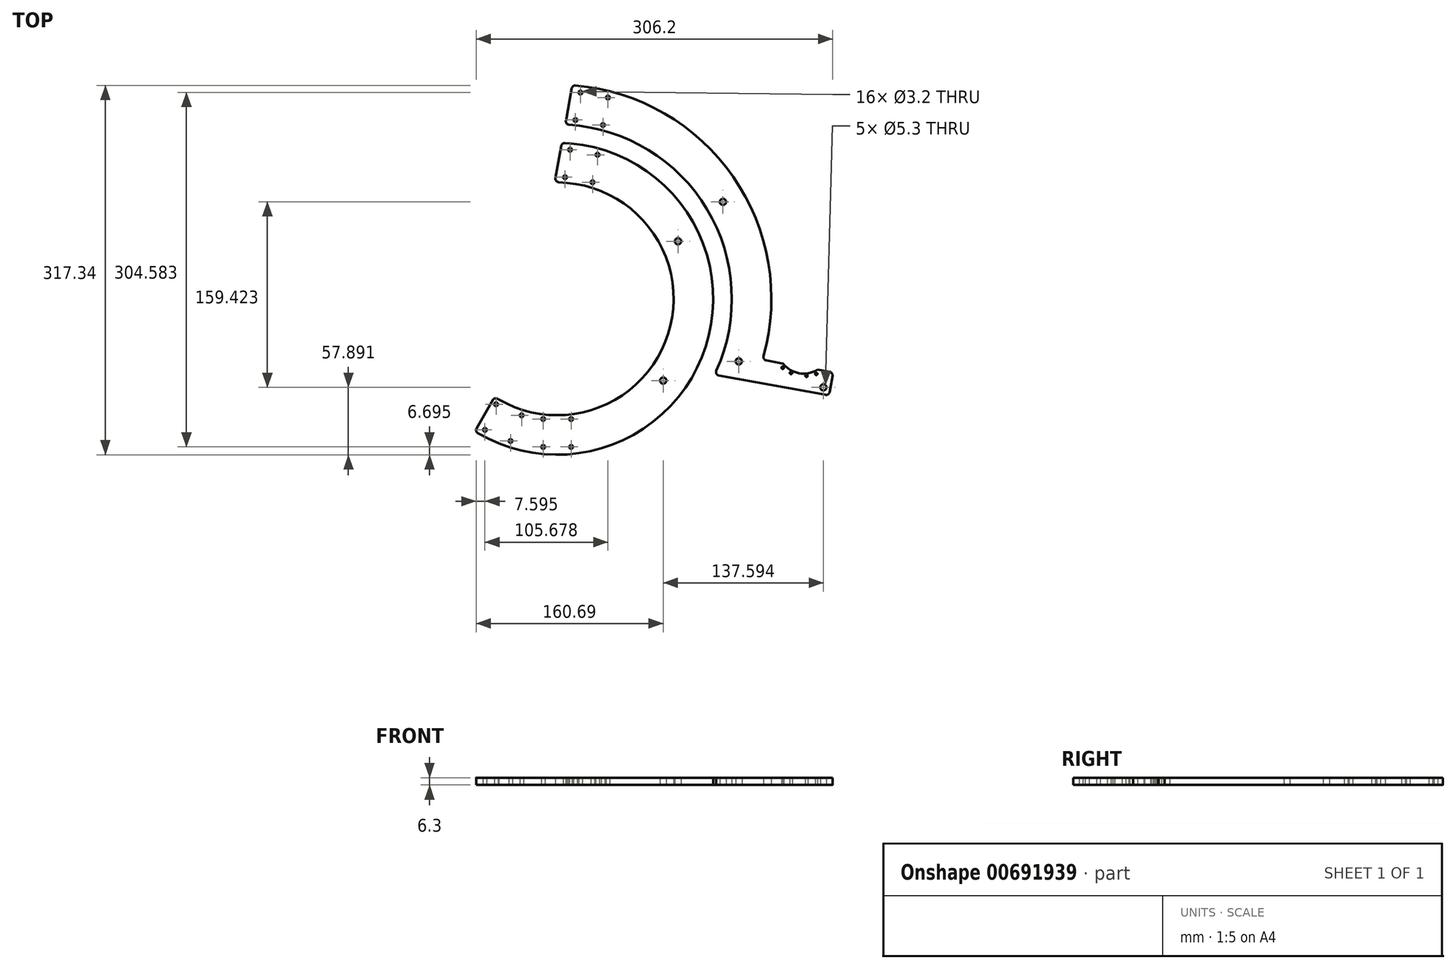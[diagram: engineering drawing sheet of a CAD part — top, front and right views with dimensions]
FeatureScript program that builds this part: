
annotation { "Feature Type Name" : "Feature", "Feature Type Description" : "" }
export const myFeature = defineFeature(function(context is Context, id is Id, definition is map)
    precondition{}
    {
        {
            var Q0;
            Q0=qCreatedBy(makeId("Top.planeOp"),FACE);
            var sketch = newSketch(context, id + "F0", { "sketchPlane" : qUnion([Q0])});
            skArc(sketch, "E0", {"start": v(-50, -86.6) * mm, "mid": v(95.37, -30.07) * mm, "end": v(8.72, 99.62) * mm});
            skLineSegment(sketch, "E1", {"start": v(11.68, 133.5) * mm, "end": v(0, 0) * mm, "construction": true});
            skLineSegment(sketch, "E2", {"start": v(-67, -116.05) * mm, "end": v(0, 0) * mm, "construction": true});
            skArc(sketch, "E3", {"start": v(11.68, 133.5) * mm, "mid": v(127.6, -40.94) * mm, "end": v(-68.16, -115.37) * mm});
            skLineSegment(sketch, "E4", {"start": v(0, 0) * mm, "end": v(-141.6, -325.67) * mm, "construction": true});
            skLineSegment(sketch, "E5", {"start": v(0, 0) * mm, "end": v(56.94, 313.3) * mm, "construction": true});
            skCircle(sketch, "E6", {"center": v(-52.47, -90.59) * mm, "radius": 1.6 * mm});
            skCircle(sketch, "E7", {"center": v(-62.04, -112.6) * mm, "radius": 1.6 * mm});
            skCircle(sketch, "E8", {"center": v(-30.47, -100.16) * mm, "radius": 1.6 * mm});
            skCircle(sketch, "E9", {"center": v(-40.04, -122.17) * mm, "radius": 1.6 * mm});
            skLineSegment(sketch, "E10", {"start": v(-76.38, -80.2) * mm, "end": v(-0.38, -113.24) * mm, "construction": true});
            skLineSegment(sketch, "E11", {"start": v(-90.91, -100.05) * mm, "end": v(-6.32, -136.83) * mm, "construction": true});
            skLineSegment(sketch, "E12", {"start": v(-105.1, -211.63) * mm, "end": v(-88.22, -172.8) * mm, "construction": true});
            skLineSegment(sketch, "E13", {"start": v(-83.02, -221.03) * mm, "end": v(-61.96, -172.6) * mm, "construction": true});
            skLineSegment(sketch, "E14", {"start": v(6.07, 129) * mm, "end": v(53.18, 120.43) * mm, "construction": true});
            skLineSegment(sketch, "E15", {"start": v(3.55, 105.06) * mm, "end": v(50.74, 96.48) * mm, "construction": true});
            skLineSegment(sketch, "E16", {"start": v(54.37, 232.05) * mm, "end": v(48.26, 198.43) * mm, "construction": true});
            skLineSegment(sketch, "E17", {"start": v(30.52, 235.08) * mm, "end": v(24.48, 201.84) * mm, "construction": true});
            skCircle(sketch, "E18", {"center": v(6.79, 104.47) * mm, "radius": 1.6 * mm});
            skCircle(sketch, "E19", {"center": v(30.4, 100.18) * mm, "radius": 1.6 * mm});
            skCircle(sketch, "E20", {"center": v(34.7, 123.8) * mm, "radius": 1.6 * mm});
            skCircle(sketch, "E21", {"center": v(11.08, 128.08) * mm, "radius": 1.6 * mm});
            skLineSegment(sketch, "E22", {"start": v(-50.4, -86.35) * mm, "end": v(-50, -86.6) * mm});
            skPoint(sketch, "E23.visualSharp", {"position": v(-53.75, -84.2) * mm});
            skLineSegment(sketch, "E24", {"start": v(11.68, 133.5) * mm, "end": v(6.78, 133.92) * mm});
            skLineSegment(sketch, "E25", {"start": v(3.56, 131.47) * mm, "end": v(-1.46, 103.8) * mm});
            skLineSegment(sketch, "E26", {"start": v(1.23, 100.27) * mm, "end": v(8.72, 99.62) * mm});
            skPoint(sketch, "E27.visualSharp", {"position": v(-2.05, 100.56) * mm});
            skArc(sketch, "E27.filletArc", {"start": v(-1.46, 103.8) * mm, "mid": v(-0.9, 101.44) * mm, "end": v(1.23, 100.27) * mm});
            skPoint(sketch, "E28.visualSharp", {"position": v(4.05, 134.16) * mm});
            skArc(sketch, "E28.filletArc", {"start": v(6.78, 133.92) * mm, "mid": v(4.7, 133.32) * mm, "end": v(3.56, 131.47) * mm});
            skPoint(sketch, "E29.visualSharp", {"position": v(-67, -116.05) * mm});
            skCircle(sketch, "E30", {"center": v(12, -103.3) * mm, "radius": 1.6 * mm});
            skCircle(sketch, "E31", {"center": v(12, -127.3) * mm, "radius": 1.6 * mm});
            skCircle(sketch, "E32.MirrorC", {"center": v(-12, -103.3) * mm, "radius": 1.6 * mm});
            skCircle(sketch, "E33.MirrorC", {"center": v(-12, -127.3) * mm, "radius": 1.6 * mm});
            skLineSegment(sketch, "E34", {"start": v(-69.24, -111.3) * mm, "end": v(-55.32, -86.94) * mm});
            skLineSegment(sketch, "E35", {"start": v(-50.4, -86.35) * mm, "end": v(-51.09, -85.9) * mm});
            skPoint(sketch, "E36.visualSharp", {"position": v(-70.7, -113.84) * mm});
            skArc(sketch, "E36.filletArc", {"start": v(-69.24, -111.3) * mm, "mid": v(-69.54, -113.55) * mm, "end": v(-68.16, -115.37) * mm});
            skArc(sketch, "E37.filletArc", {"start": v(-51.09, -85.9) * mm, "mid": v(-53.42, -85.51) * mm, "end": v(-55.32, -86.94) * mm});
            skCircle(sketch, "E38", {"center": v(103.82, 49.47) * mm, "radius": 2.65 * mm});
            skCircle(sketch, "E39", {"center": v(91.05, -70.25) * mm, "radius": 2.65 * mm});
            skSolve(sketch);
        }
        {
            var Q0;
            {var subQ0=sQuery(id+"F0.wireOp",EDGE,"E0");Q0=makeQuery(id+"F0.imprint","IMPRINT",FACE,{"disambiguationData":[TD([[makeQuery(id+"F0.imprint","IMPRINT",EDGE,{"derivedFrom":subQ0}),-1.0]])]});}
            var Q1;
            {var subQ1=sQuery(id+"F0.wireOp",EDGE,"5APrBCez-5t1e-EGUt-UYpU-bVJNniEtidSN");Q1=makeQuery(id+"F0.imprint","IMPRINT",FACE,{"disambiguationData":[TD([[makeQuery(id+"F0.imprint","IMPRINT",EDGE,{"derivedFrom":subQ1}),-1.0]])]});}
            var Q2;
            {var subQ7=sQuery(id+"F0.wireOp",EDGE,"E24");Q2=makeQuery(id+"F0.imprint","IMPRINT",FACE,{"disambiguationData":[TD([[makeQuery(id+"F0.imprint","IMPRINT",EDGE,{"derivedFrom":subQ7}),1.0]])]});}
            var Q3;
            {var subQ5=sQuery(id+"F0.wireOp",EDGE,"E22");Q3=makeQuery(id+"F0.imprint","IMPRINT",FACE,{"disambiguationData":[TD([[makeQuery(id+"F0.imprint","IMPRINT",EDGE,{"derivedFrom":subQ5}),-1.0]])]});}
            extrude(context, id + "F1", {"entities" : qUnion([Q0, Q1, Q2, Q3]), "depth" : 6.3 * mm, "offsetDistance" : 25 * mm});
        }
        {
            var Q0;
            Q0=qCreatedBy(makeId("Top.planeOp"),FACE);
            var sketch = newSketch(context, id + "F2", { "sketchPlane" : qUnion([Q0])});
            skArc(sketch, "E40", {"start": v(10.26, 149.65) * mm, "mid": v(128.72, 77.01) * mm, "end": v(136.72, -61.71) * mm});
            skArc(sketch, "E41.0", {"start": v(15.75, 183.32) * mm, "mid": v(151.12, 104.98) * mm, "end": v(177.3, -49.22) * mm});
            skLineSegment(sketch, "E42", {"start": v(12.54, 180.87) * mm, "end": v(7.5, 153.18) * mm});
            skLineSegment(sketch, "E43", {"start": v(138.91, -65.9) * mm, "end": v(230.52, -82.55) * mm});
            skLineSegment(sketch, "E44", {"start": v(234.01, -80.13) * mm, "end": v(236.51, -66.36) * mm});
            skLineSegment(sketch, "E45", {"start": v(234.1, -62.87) * mm, "end": v(223.5, -60.94) * mm});
            skArc(sketch, "E46", {"start": v(193.98, -55.58) * mm, "mid": v(207.71, -63.9) * mm, "end": v(223.5, -60.94) * mm});
            skPoint(sketch, "E47.visualSharp", {"position": v(233.48, -83.08) * mm});
            skArc(sketch, "E47.filletArc", {"start": v(230.52, -82.55) * mm, "mid": v(232.77, -82.06) * mm, "end": v(234.01, -80.13) * mm});
            skPoint(sketch, "E48.visualSharp", {"position": v(237.05, -63.4) * mm});
            skArc(sketch, "E48.filletArc", {"start": v(236.51, -66.36) * mm, "mid": v(236.03, -64.11) * mm, "end": v(234.1, -62.87) * mm});
            skPoint(sketch, "E49.visualSharp", {"position": v(135.09, -65.2) * mm});
            skArc(sketch, "E49.filletArc", {"start": v(136.72, -61.71) * mm, "mid": v(136.8, -64.34) * mm, "end": v(138.91, -65.9) * mm});
            skArc(sketch, "E50.filletArc", {"start": v(177.3, -49.22) * mm, "mid": v(177.64, -51.62) * mm, "end": v(179.65, -52.98) * mm});
            skPoint(sketch, "E51.visualSharp", {"position": v(6.9, 149.84) * mm});
            skArc(sketch, "E51.filletArc", {"start": v(7.5, 153.18) * mm, "mid": v(8.1, 150.8) * mm, "end": v(10.26, 149.65) * mm});
            skPoint(sketch, "E52.visualSharp", {"position": v(13.03, 183.54) * mm});
            skArc(sketch, "E52.filletArc", {"start": v(15.75, 183.32) * mm, "mid": v(13.67, 182.72) * mm, "end": v(12.54, 180.87) * mm});
            skLineSegment(sketch, "E53", {"start": v(0, 0) * mm, "end": v(288.03, -52.34) * mm, "construction": true});
            skLineSegment(sketch, "E54", {"start": v(172.85, -31.41) * mm, "end": v(241, -43.8) * mm, "construction": true});
            skLineSegment(sketch, "E55", {"start": v(0, 0) * mm, "end": v(36.35, 200.01) * mm, "construction": true});
            skLineSegment(sketch, "E56", {"start": v(4.18, 155.76) * mm, "end": v(56.02, 146.34) * mm, "construction": true});
            skLineSegment(sketch, "E57", {"start": v(7.9, 179.48) * mm, "end": v(53.9, 171.12) * mm, "construction": true});
            skCircle(sketch, "E58", {"center": v(20.02, 177.28) * mm, "radius": 1.6 * mm});
            skCircle(sketch, "E59", {"center": v(15.73, 153.66) * mm, "radius": 1.6 * mm});
            skCircle(sketch, "E60.MirrorC", {"center": v(43.63, 172.99) * mm, "radius": 1.6 * mm});
            skCircle(sketch, "E61.MirrorC", {"center": v(39.34, 149.37) * mm, "radius": 1.6 * mm});
            skCircle(sketch, "E62", {"center": v(214.17, -66.16) * mm, "radius": 1 * mm});
            skCircle(sketch, "E63", {"center": v(222.51, -64.48) * mm, "radius": 1 * mm});
            skLineSegment(sketch, "E64.trimOffspring", {"start": v(193.98, -55.58) * mm, "end": v(179.65, -52.98) * mm});
            skCircle(sketch, "E65", {"center": v(156, -53.76) * mm, "radius": 2.65 * mm});
            skCircle(sketch, "E66", {"center": v(142.42, 83.31) * mm, "radius": 2.65 * mm});
            skCircle(sketch, "E67", {"center": v(228.64, -76.1) * mm, "radius": 2.65 * mm});
            skLineSegment(sketch, "E68", {"start": v(21.94, 187.86) * mm, "end": v(14.2, 145.22) * mm, "construction": true});
            skLineSegment(sketch, "E69", {"start": v(207.71, -63.9) * mm, "end": v(205.16, -77.94) * mm, "construction": true});
            skCircle(sketch, "E70.MirrorC", {"center": v(200.87, -63.75) * mm, "radius": 1 * mm});
            skCircle(sketch, "E71.MirrorC", {"center": v(193.66, -59.24) * mm, "radius": 1 * mm});
            skSolve(sketch);
        }
        {
            var Q0;
            {var subQ5=sQuery(id+"F2.wireOp",EDGE,"E40");Q0=makeQuery(id+"F2.imprint","IMPRINT",FACE,{"disambiguationData":[TD([[makeQuery(id+"F2.imprint","IMPRINT",EDGE,{"derivedFrom":subQ5}),1.0]])]});}
            var Q1;
            {var subQ4=sQuery(id+"F2.wireOp",EDGE,"E44");Q1=makeQuery(id+"F2.imprint","IMPRINT",FACE,{"disambiguationData":[TD([[makeQuery(id+"F2.imprint","IMPRINT",EDGE,{"derivedFrom":subQ4}),1.0]])]});}
            extrude(context, id + "F3", {"entities" : qUnion([Q0, Q1]), "depth" : 6.3 * mm, "offsetDistance" : 25 * mm});
        }
    });
